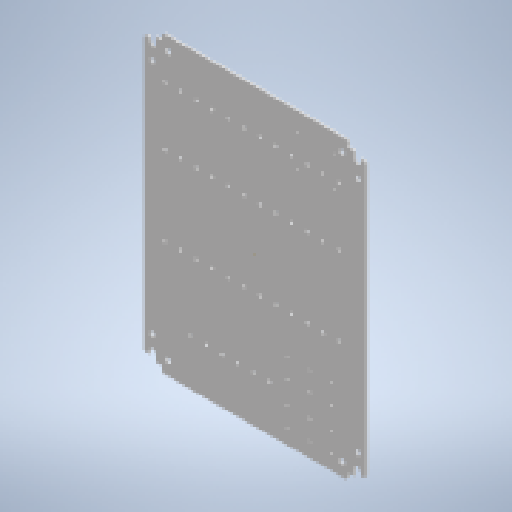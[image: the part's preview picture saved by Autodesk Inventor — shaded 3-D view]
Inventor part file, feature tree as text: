
AUTODESK INVENTOR PART (.ipt)
format: ipt  version: 2023 (Build 270158030, 158C)  size: 537,088 bytes
history: native  units: mm
features: reference x18, other x15, extrude x4, sketch x4, mirror x2
ambient origin geometry x8: Origin, YZ Plane, XZ Plane, XY Plane, X Axis, Y Axis, Z Axis, Center Point
bodies: Solid1 (feature_tree)
feature tree (43):
  other  "Blocks"
  extrude  "Extrusion1"  Depth=465.0mm
  extrude  "Extrusion2"  Depth=175.0mm
  mirror  "Mirror1"
  mirror  "Mirror2"
  extrude  "Extrusion3"  Depth=465.0mm
  extrude  "Extrusion4"  Depth=28.5mm
  sketch  "Sketch1"  dims[d0=350.0mm d1=465.0mm]
  sketch  "Sketch3"  dims[d2=232.5mm d3=175.0mm]
  sketch  "Sketch4"  dims[d4=3.0mm d5=0.0mm d7=465.0mm]
  reference  "Reference1"
  reference  "Reference2"
  reference  "Reference3"
  reference  "Reference4"
  reference  "Reference5"
  reference  "Reference6"
  reference  "Reference7"
  reference  "Reference8"
  reference  "Reference9"
  reference  "Reference10"
  reference  "Reference11"
  reference  "Reference12"
  reference  "Reference13"
  reference  "Reference14"
  reference  "Reference15"
  reference  "Reference16"
  reference  "Reference17"
  reference  "Reference18"
  sketch  "Sketch5"  dims[d8=350.0mm d9=28.5mm d10=10.0mm d11=6.0mm d12=19.0mm d14=5.0mm d15=11.0mm d16=45.0deg d17=3.0mm d18=3.0mm d19=45.0deg d20=0.0mm d21=0.0mm d22=8.4mm d23=13.0mm d24=13.5mm d25=45.5mm d26=37.5mm d27=21.0mm d28=5.2mm d29=5.8mm d30=5.8mm d31=25.0mm d32=120.0mm d34=25.0mm d35=20.0mm d37=125.0mm d40=5.2mm d41=5.8mm d42=60.0mm d44=25.0mm d45=10.0mm d47=10.0mm d49=3.2mm d50=30.0mm d52=35.0mm d53=20.0mm d55=97.5mm d58=20.0mm d60=92.0mm d61=120.0mm d63=25.0mm d66=0.0mm d67=0.0mm d68=4.0mm d69=15.0mm d70=145.0mm d71=100.0mm d73=25.0mm d74=10.0mm d76=10.0mm d81=50.0mm d83=25.0mm d84=10.0mm d86=10.0mm d88=1.0mm d89=0.0mm d142=2.0mm d146=1.0mm d148=19.5mm d150=1.0mm d155=50.0mm d157=19.5mm d158=10.0mm d160=10.0mm d165=100.0mm d167=10.0mm d169=50.0mm d171=10.0mm d173=50.0mm d175=10.0mm d176=50.0mm d177=62.0mm d178=20.0mm d179=1.0mm d180=1.0mm d181=1.0mm d182=1.0mm d183=1.0mm d184=1.0mm]
  other  "high voltage"
  other  "<userpath>\Documents\0004-inventor\Inventor_Projects\electronics-enclosure\enclosure.iam"
  other  "enclosure.iam"
  other  "Raspberry Pi 4 Model B:1"
  other  "PCB, RPi4ModelB_1"
  other  "DIN-rail:1"
  other  "DIN-rail-short:1"
  other  "solid state relay_MIR:1"
  other  "solid state relay_MIR:2"
  other  "solid state relay_MIR:3"
  other  "solid state relay:1"
  other  "solid state relay:3"
  other  "solid state relay:4"
  other  "high voltage:1"
